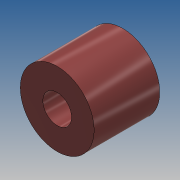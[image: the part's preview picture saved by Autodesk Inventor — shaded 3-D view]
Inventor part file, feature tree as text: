
AUTODESK INVENTOR PART (.ipt)
format: ipt  version: 2017 (Build 210142000, 142)  size: 86,528 bytes
history: native  units: mm
features: other x1, extrude x1, sketch x1
ambient origin geometry x8: Origin, YZ Plane, XZ Plane, XY Plane, X Axis, Y Axis, Z Axis, Center Point
bodies: Body1 (feature_tree)
feature tree (3):
  other  "Sólido1"
  extrude  "Extrusión1"  Depth=8.0mm
  sketch  "Boceto1"  dims[d0=3.5mm d1=9.0mm d2=8.0mm d3=0.0mm]
